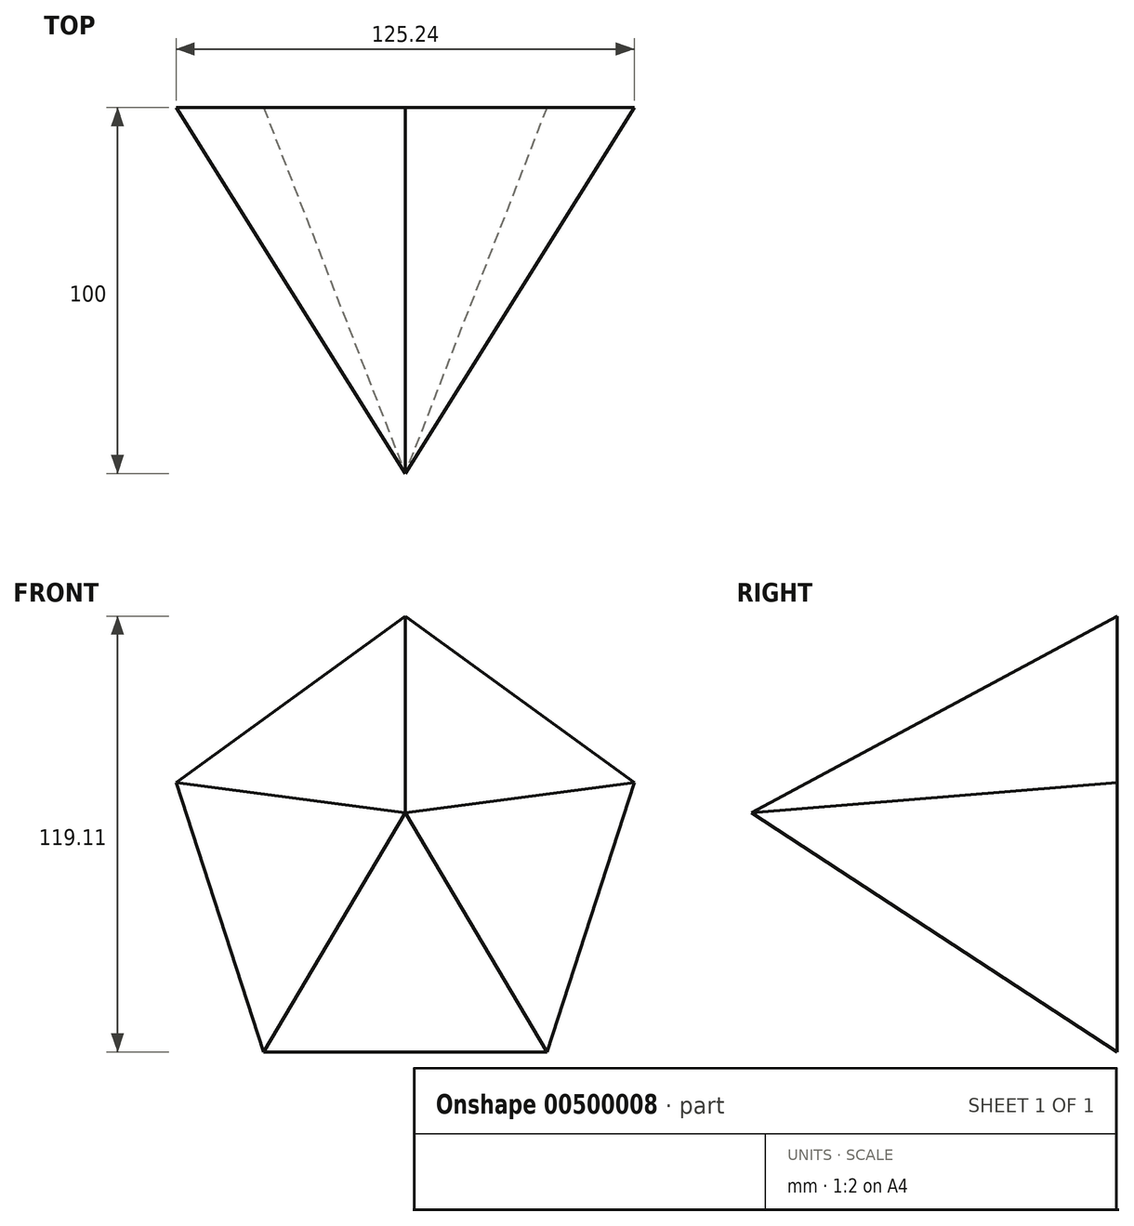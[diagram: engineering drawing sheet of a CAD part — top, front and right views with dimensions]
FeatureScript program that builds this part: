
annotation { "Feature Type Name" : "Feature", "Feature Type Description" : "" }
export const myFeature = defineFeature(function(context is Context, id is Id, definition is map)
    precondition{}
    {
        {
            var Q0;
            Q0=qCreatedBy(makeId("Front.planeOp"),FACE);
            var sketch = newSketch(context, id + "F0", { "sketchPlane" : qUnion([Q0])});
            skCircle(sketch, "E0.cCircle", {"center": v(0, 0) * mm, "radius": 65.84 * mm, "construction": true});
            skLineSegment(sketch, "E0.0", {"start": v(-62.62, 20.35) * mm, "end": v(0, 65.84) * mm});
            skLineSegment(sketch, "E0.1", {"start": v(0, 65.84) * mm, "end": v(62.62, 20.35) * mm});
            skLineSegment(sketch, "E0.2", {"start": v(62.62, 20.35) * mm, "end": v(38.7, -53.27) * mm});
            skLineSegment(sketch, "E0.3", {"start": v(38.7, -53.27) * mm, "end": v(-38.7, -53.27) * mm});
            skLineSegment(sketch, "E0.4", {"start": v(-38.7, -53.27) * mm, "end": v(-62.62, 20.35) * mm});
            skSolve(sketch);
        }
        {
            var Q0;
            Q0=qCreatedBy(makeId("Front.planeOp"),FACE);
            cPlane(context, id + "F1", {"entities" : qUnion([Q0]), "cplaneType" : CPlaneType.OFFSET, "offset" : 100 * mm, "width" : 150 * mm, "height" : 150 * mm});
        }
        {
            var Q0;
            Q0=qCreatedBy(id+"F1.planeOp",FACE);
            var sketch = newSketch(context, id + "F2", { "sketchPlane" : qUnion([Q0])});
            skPoint(sketch, "E1", {"position": v(0, 12.07) * mm});
            skSolve(sketch);
        }
        {
            var Q0;
            Q0=makeQuery(id+"F0.imprint","IMPRINT",FACE,{"disambiguationData":[TD([[makeQuery(id+"F0.imprint","IMPRINT",EDGE,{"derivedFrom":sQuery(id+"F0.wireOp",EDGE,"E0.0")}),-1.0]])]});
            var Q1;
            Q1=sQuery(id+"F2.wireOp",VERTEX,"E1");
            loft(context, id + "F3", {"sheetProfilesArray" : [{ "sheetProfileEntities" : qUnion([Q0]) }, { "sheetProfileEntities" : qUnion([Q1]) }]});
        }
    });
